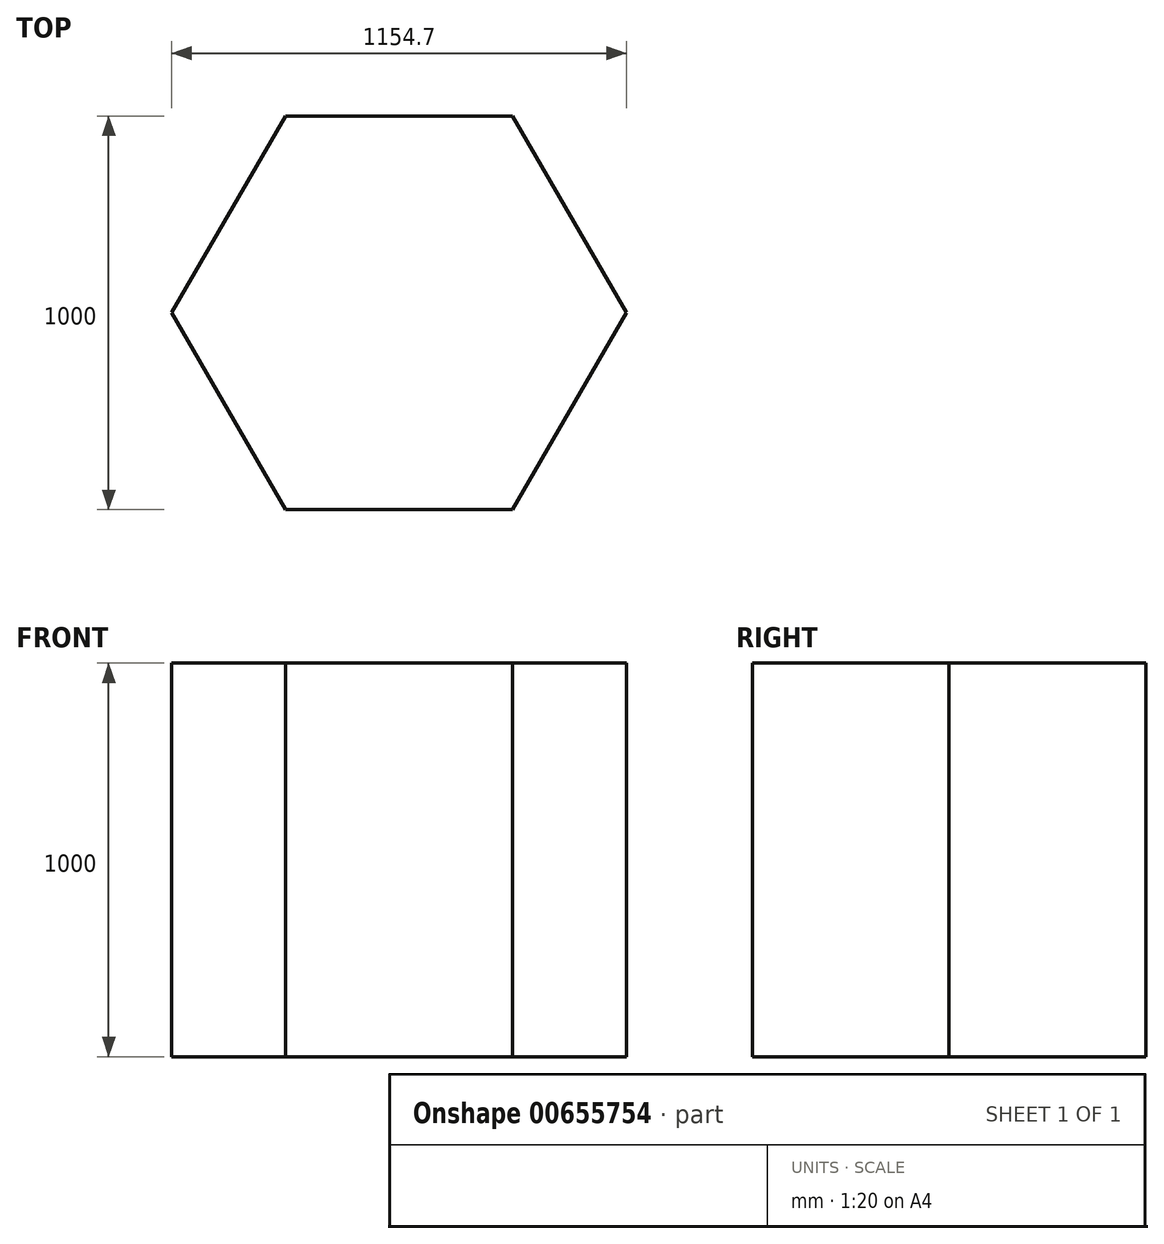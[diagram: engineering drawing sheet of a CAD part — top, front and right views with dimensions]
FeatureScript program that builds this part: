
annotation { "Feature Type Name" : "Feature", "Feature Type Description" : "" }
export const myFeature = defineFeature(function(context is Context, id is Id, definition is map)
    precondition{}
    {
        {
            var Q0;
            Q0=qCreatedBy(makeId("Top.planeOp"),FACE);
            var sketch = newSketch(context, id + "F0", { "sketchPlane" : qUnion([Q0])});
            skCircle(sketch, "E0.cCircle", {"center": v(0, 0) * mm, "radius": 500 * mm, "construction": true});
            skLineSegment(sketch, "E0.0", {"start": v(-288.68, 500) * mm, "end": v(288.68, 500) * mm});
            skLineSegment(sketch, "E0.1", {"start": v(288.68, 500) * mm, "end": v(577.35, 0) * mm});
            skLineSegment(sketch, "E0.2", {"start": v(577.35, 0) * mm, "end": v(288.68, -500) * mm});
            skLineSegment(sketch, "E0.3", {"start": v(288.68, -500) * mm, "end": v(-288.68, -500) * mm});
            skLineSegment(sketch, "E0.4", {"start": v(-288.68, -500) * mm, "end": v(-577.35, 0) * mm});
            skLineSegment(sketch, "E0.5", {"start": v(-577.35, 0) * mm, "end": v(-288.68, 500) * mm});
            skPoint(sketch, "E0.0.midPoint", {"position": v(0, 500) * mm});
            skSolve(sketch);
        }
        {
            var Q0;
            Q0 = qSketchRegion(id + "F0", true);
            extrude(context, id + "F1", {"entities" : qUnion([Q0]), "depth" : 1000 * mm, "offsetDistance" : 25 * mm});
        }
    });
